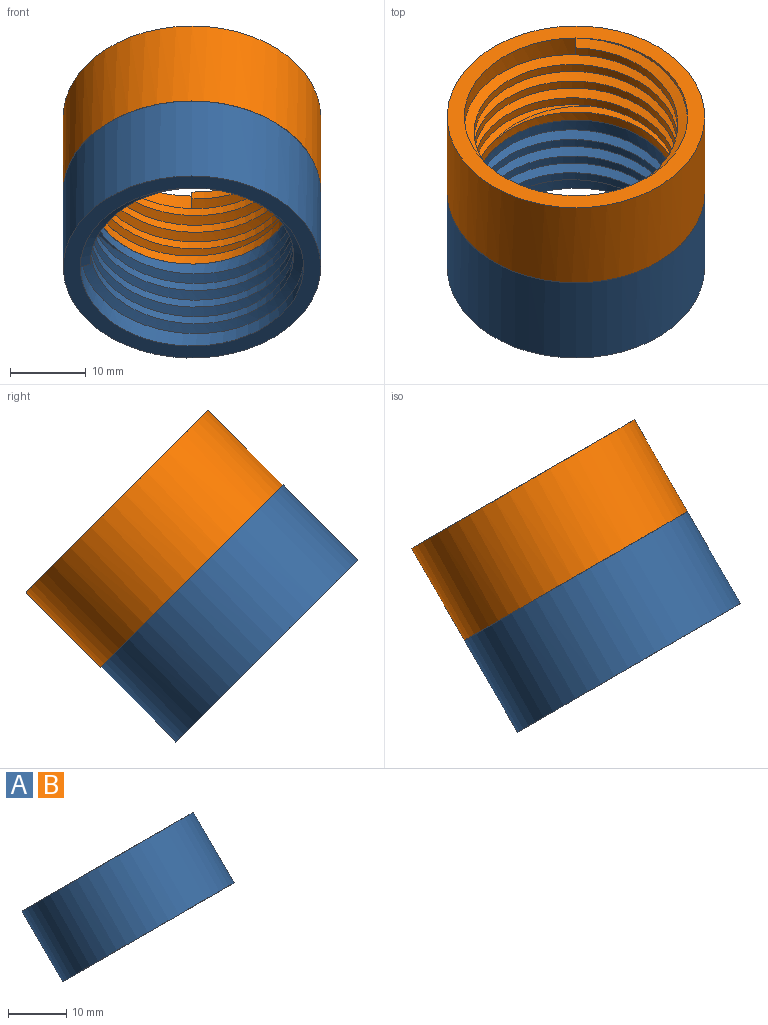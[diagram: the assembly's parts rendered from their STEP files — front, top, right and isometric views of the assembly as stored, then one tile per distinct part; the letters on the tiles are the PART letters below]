
ASSEMBLY  parts=2 mates=1
PART A: 13 faces, bbox 34.3x34.3x34.3 mm
  f0: cylinder r=14.75mm len=29.7mm, axis (0,0.71,0.71), area 350.4mm2, adj f2,f3,f4,f5,f12
  f1: cylinder r=17mm len=34mm, axis (0,0.71,0.71), area 1495.4mm2, adj f2,f11
  f2: plane 34x24.04mm, normal (0,-0.71,-0.71), area 224.4mm2, adj f0,f1
  f3: plane 1.7x1.7mm, normal (0,0.71,-0.71), area 2.4mm2, adj f0,f4,f5,f6
  f4: bspline ~29.57x29.57mm, area 418.9mm2, adj f0,f3,f6,f7,f8,f9,f12
  f5: bspline ~31.76x29.57mm, area 493.6mm2, adj f0,f3,f6,f7,f8,f9,f10,f12
  f6: cylinder r=13.45mm len=25.78mm, axis (0,0.71,0.71), area 47.8mm2, adj f3,f4,f5,f7
  f7: cylinder r=13.45mm len=26.9mm, axis (0,0.71,0.71), area 109.9mm2, adj f4,f5,f6,f8
  f8: cylinder r=13.45mm len=26.9mm, axis (0,0.71,0.71), area 109.9mm2, adj f4,f5,f7,f9
  f9: cylinder r=13.45mm len=26.9mm, axis (0,0.71,0.71), area 109.8mm2, adj f4,f5,f8,f10
  f10: cylinder r=13.45mm len=26.9mm, axis (0,0.71,0.71), area 149.9mm2, adj f5,f9,f11,f12
  f11: plane 34x24.04mm, normal (0,0.71,0.71), area 339.6mm2, adj f1,f10
  f12: plane 27.23x18.24mm, normal (0,-0.71,-0.71), area 46mm2, adj f0,f4,f5,f10
PART B: same geometry as A
PLACE A t=(-159.36,65.01,-21.19)mm
PLACE B rot(axis=(-0.71,0.5,-0.5),180deg) t=(134.83,275.15,-227.09)mm
MATE fastened B.f0 <-> A.f0  axis (0,-0.71,-0.71) through (134.83,66.07,-20.13)mm
